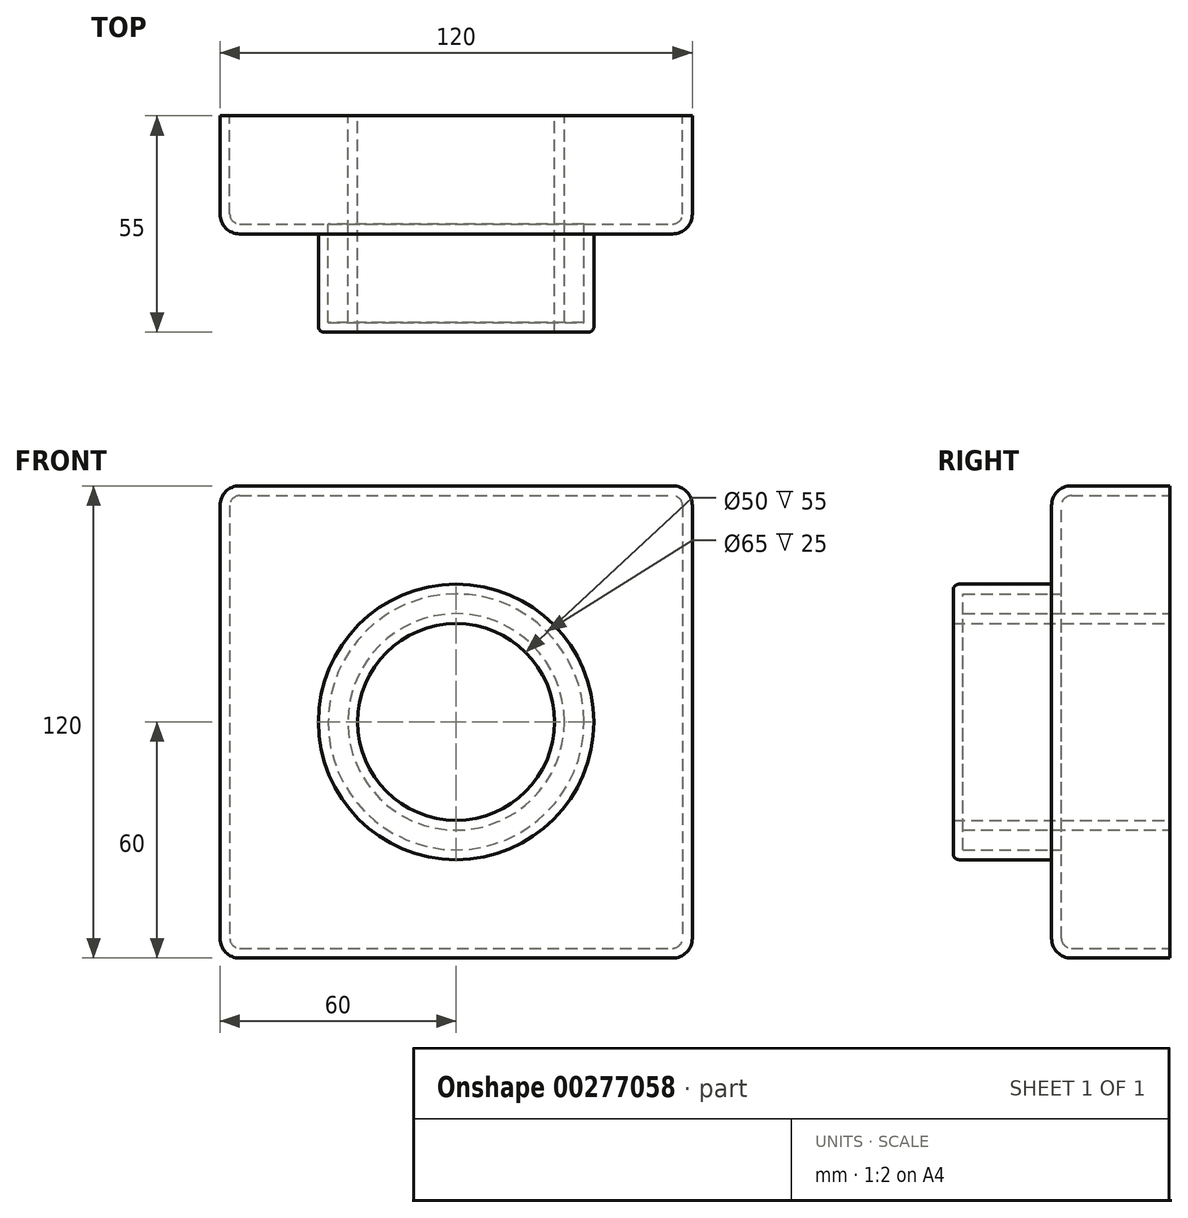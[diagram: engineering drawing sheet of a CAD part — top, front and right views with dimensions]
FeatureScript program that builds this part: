
annotation { "Feature Type Name" : "Feature", "Feature Type Description" : "" }
export const myFeature = defineFeature(function(context is Context, id is Id, definition is map)
    precondition{}
    {
        {
            var Q0;
            Q0=qCreatedBy(makeId("Front.planeOp"),FACE);
            var sketch = newSketch(context, id + "F0", { "sketchPlane" : qUnion([Q0])});
            skLineSegment(sketch, "E0.bottom", {"start": v(-60, 60) * mm, "end": v(60, 60) * mm});
            skLineSegment(sketch, "E0.top", {"start": v(-60, -60) * mm, "end": v(60, -60) * mm});
            skLineSegment(sketch, "E0.left", {"start": v(-60, 60) * mm, "end": v(-60, -60) * mm});
            skLineSegment(sketch, "E0.right", {"start": v(60, 60) * mm, "end": v(60, -60) * mm});
            skPoint(sketch, "E0.middle", {"position": v(0, 0) * mm});
            skSolve(sketch);
        }
        {
            var Q0;
            Q0=makeQuery(id+"F0.imprint","IMPRINT",FACE,{"disambiguationData":[TD([[makeQuery(id+"F0.imprint","IMPRINT",EDGE,{"derivedFrom":sQuery(id+"F0.wireOp",EDGE,"E0.bottom")}),-1.0]])]});
            extrude(context, id + "F1", {"entities" : qUnion([Q0]), "depth" : 30 * mm});
        }
        {
            var Q0;
            Q0=makeQuery(id+"F1.opExtrude","CAP_FACE",FACE,{"disambiguationData":[OSD([sQuery(id+"F0.wireOp",EDGE,"E0.bottom"),sQuery(id+"F0.wireOp",EDGE,"E0.top"),sQuery(id+"F0.wireOp",EDGE,"E0.left"),sQuery(id+"F0.wireOp",EDGE,"E0.right")])],"isStart":false});
            var sketch = newSketch(context, id + "F2", { "sketchPlane" : qUnion([Q0])});
            skCircle(sketch, "E1", {"center": v(0, 0) * mm, "radius": 35 * mm});
            skCircle(sketch, "E2", {"center": v(0, 0) * mm, "radius": 25 * mm});
            skSolve(sketch);
        }
        {
            var Q0;
            Q0=makeQuery(id+"F2.imprint","IMPRINT",FACE,{"disambiguationData":[TD([[makeQuery(id+"F2.imprint","IMPRINT",EDGE,{"derivedFrom":sQuery(id+"F2.wireOp",EDGE,"E1")}),1.0]])]});
            extrude(context, id + "F3", {"entities" : qUnion([Q0]), "operationType" : NewBodyOperationType.ADD, "depth" : 25 * mm});
        }
        {
            var Q0;
            Q0=makeQuery(id+"F1.opExtrude","CAP_FACE",FACE,{"disambiguationData":[OSD([sQuery(id+"F0.wireOp",EDGE,"E0.bottom"),sQuery(id+"F0.wireOp",EDGE,"E0.top"),sQuery(id+"F0.wireOp",EDGE,"E0.left"),sQuery(id+"F0.wireOp",EDGE,"E0.right")])],"isStart":true});
            var sketch = newSketch(context, id + "F4", { "sketchPlane" : qUnion([Q0])});
            skCircle(sketch, "E3", {"center": v(0, 0) * mm, "radius": 25 * mm});
            skSolve(sketch);
        }
        {
            var Q0;
            Q0 = qSketchRegion(id + "F4", true);
            extrude(context, id + "F5", {"entities" : qUnion([Q0]), "operationType" : NewBodyOperationType.REMOVE, "endBound" : BoundingType.THROUGH_ALL, "oppositeDirection" : true, "depth" : 25 * mm});
        }
        {
            var Q0;
            Q0=makeQuery(id+"F1.opExtrude","SWEPT_EDGE",EDGE,{"disambiguationData":[OSD([sQuery(id+"F0.wireOp",EDGE,"E0.bottom"),sQuery(id+"F0.wireOp",EDGE,"E0.right")])]});
            var Q1;
            Q1=makeQuery(id+"F1.opExtrude","SWEPT_EDGE",EDGE,{"disambiguationData":[OSD([sQuery(id+"F0.wireOp",EDGE,"E0.top"),sQuery(id+"F0.wireOp",EDGE,"E0.right")])]});
            var Q2;
            Q2=makeQuery(id+"F1.opExtrude","CAP_EDGE",EDGE,{"disambiguationData":[OSD([sQuery(id+"F0.wireOp",EDGE,"E0.right")])],"isStart":false});
            var Q3;
            Q3=makeQuery(id+"F1.opExtrude","CAP_EDGE",EDGE,{"disambiguationData":[OSD([sQuery(id+"F0.wireOp",EDGE,"E0.top")])],"isStart":false});
            var Q4;
            Q4=makeQuery(id+"F1.opExtrude","CAP_EDGE",EDGE,{"disambiguationData":[OSD([sQuery(id+"F0.wireOp",EDGE,"E0.left")])],"isStart":false});
            var Q5;
            Q5=makeQuery(id+"F1.opExtrude","CAP_EDGE",EDGE,{"disambiguationData":[OSD([sQuery(id+"F0.wireOp",EDGE,"E0.bottom")])],"isStart":false});
            var Q6;
            Q6=makeQuery(id+"F1.opExtrude","SWEPT_EDGE",EDGE,{"disambiguationData":[OSD([sQuery(id+"F0.wireOp",EDGE,"E0.bottom"),sQuery(id+"F0.wireOp",EDGE,"E0.left")])]});
            var Q7;
            Q7=makeQuery(id+"F1.opExtrude","SWEPT_EDGE",EDGE,{"disambiguationData":[OSD([sQuery(id+"F0.wireOp",EDGE,"E0.top"),sQuery(id+"F0.wireOp",EDGE,"E0.left")])]});
            var Q8;
            Q8=makeQuery(id+"F3.opExtrude","CAP_EDGE",EDGE,{"disambiguationData":[OSD([sQuery(id+"F2.wireOp",EDGE,"E1")])],"isStart":true});
            fillet(context, id + "F6", {"entities" : qUnion([Q0, Q1, Q2, Q3, Q4, Q5, Q6, Q7, Q8]), "radius" : 5 * mm, "tangentPropagation" : true, "allowEdgeOverflow" : false});
        }
        {
            var Q0;
            Q0=makeQuery(id+"F3.opExtrude","CAP_EDGE",EDGE,{"disambiguationData":[OSD([sQuery(id+"F2.wireOp",EDGE,"E1")])],"isStart":false});
            fillet(context, id + "F7", {"entities" : qUnion([Q0]), "radius" : 1.5 * mm, "tangentPropagation" : true, "allowEdgeOverflow" : false});
        }
        {
            var Q0;
            Q0=makeQuery(id+"F1.opExtrude","CAP_FACE",FACE,{"disambiguationData":[OSD([sQuery(id+"F0.wireOp",EDGE,"E0.bottom"),sQuery(id+"F0.wireOp",EDGE,"E0.top"),sQuery(id+"F0.wireOp",EDGE,"E0.left"),sQuery(id+"F0.wireOp",EDGE,"E0.right")])],"isStart":true});
            shell(context, id + "F8", {"entities" : qUnion([Q0]), "thickness" : 2.5 * mm});
        }
    });
